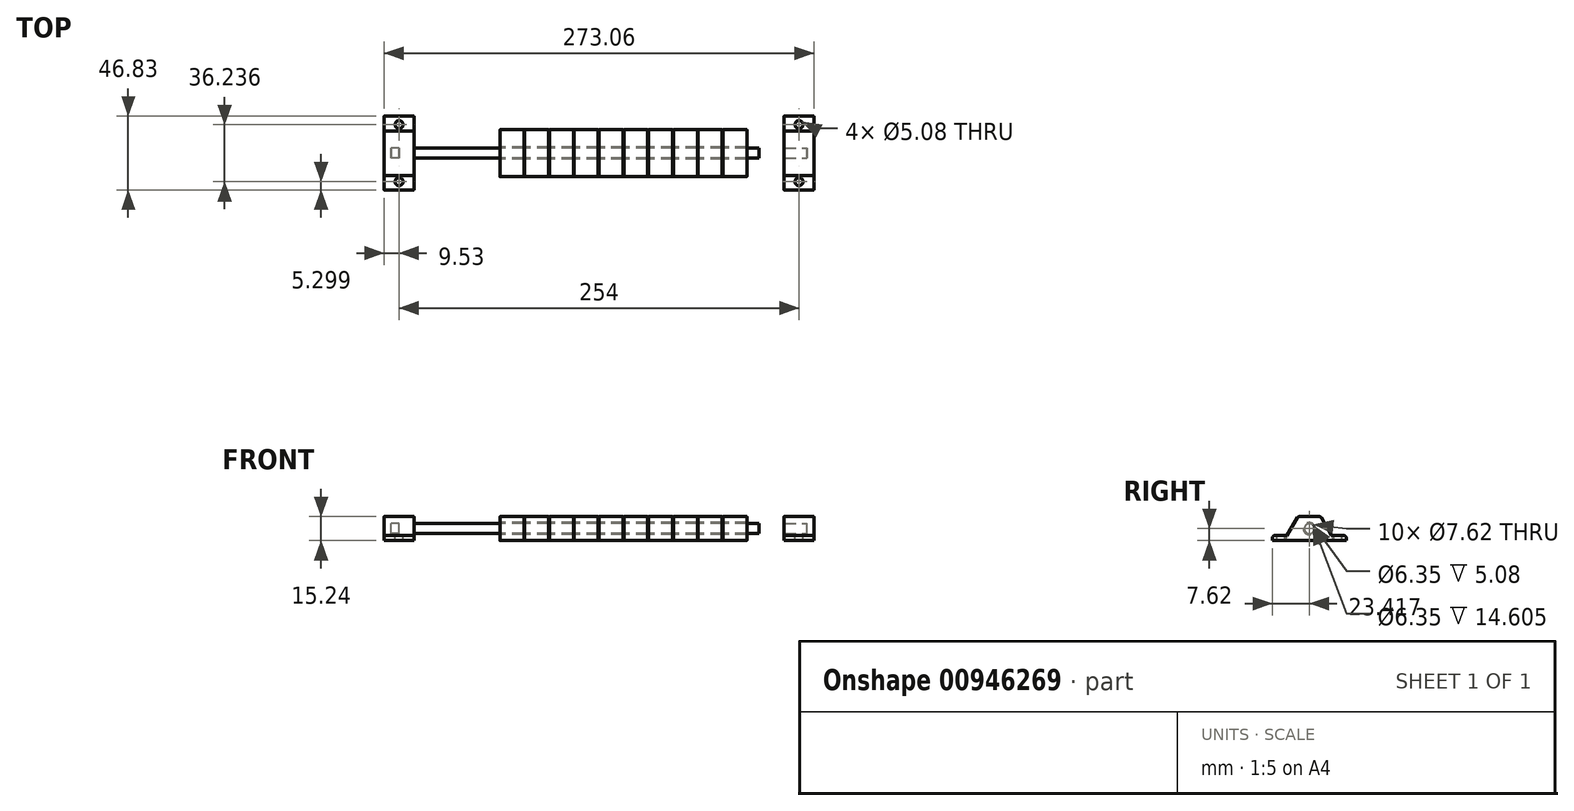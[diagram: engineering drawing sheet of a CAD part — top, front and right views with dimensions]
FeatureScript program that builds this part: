
annotation { "Feature Type Name" : "Feature", "Feature Type Description" : "" }
export const myFeature = defineFeature(function(context is Context, id is Id, definition is map)
    precondition{}
    {
        {
            var Q0;
            Q0=qCreatedBy(makeId("Right.planeOp"),FACE);
            var sketch = newSketch(context, id + "F0", { "sketchPlane" : qUnion([Q0])});
            skLineSegment(sketch, "E0", {"start": v(-49.8, 0) * mm, "end": v(-18.06, 0) * mm});
            skLineSegment(sketch, "E1", {"start": v(-18.06, 0) * mm, "end": v(-26.86, 15.24) * mm});
            skLineSegment(sketch, "E2", {"start": v(-26.86, 15.24) * mm, "end": v(-41, 15.24) * mm});
            skLineSegment(sketch, "E3", {"start": v(-41, 15.24) * mm, "end": v(-49.8, 0) * mm});
            skCircle(sketch, "E4", {"center": v(-33.93, 7.62) * mm, "radius": 3.81 * mm});
            skPoint(sketch, "E4.centerSnap0", {"position": v(-33.93, 15.24) * mm});
            skSolve(sketch);
        }
        {
            var Q0;
            Q0=makeQuery(id+"F0.imprint","IMPRINT",FACE,{"disambiguationData":[TD([[makeQuery(id+"F0.imprint","IMPRINT",EDGE,{"derivedFrom":sQuery(id+"F0.wireOp",EDGE,"E0")}),1.0]])]});
            extrude(context, id + "F1", {"entities" : qUnion([Q0]), "depth" : 15.24 * mm, "offsetDistance" : 25.4 * mm});
        }
        {
            var Q0;
            Q0=makeQuery(id+"F1.opExtrude","SWEPT_EDGE",EDGE,{"disambiguationData":[OSD([sQuery(id+"F0.wireOp",EDGE,"E2"),sQuery(id+"F0.wireOp",EDGE,"E3")])]});
            var Q1;
            Q1=makeQuery(id+"F1.opExtrude","SWEPT_EDGE",EDGE,{"disambiguationData":[OSD([sQuery(id+"F0.wireOp",EDGE,"E1"),sQuery(id+"F0.wireOp",EDGE,"E2")])]});
            var Q2;
            Q2=makeQuery(id+"F1.opExtrude","SWEPT_EDGE",EDGE,{"disambiguationData":[OSD([sQuery(id+"F0.wireOp",EDGE,"E0"),sQuery(id+"F0.wireOp",EDGE,"E1")])]});
            var Q3;
            Q3=makeQuery(id+"F1.opExtrude","SWEPT_EDGE",EDGE,{"disambiguationData":[OSD([sQuery(id+"F0.wireOp",EDGE,"E0"),sQuery(id+"F0.wireOp",EDGE,"E3")])]});
            fillet(context, id + "F2", {"entities" : qUnion([Q0, Q1, Q2, Q3]), "tangentPropagation" : true, "radius" : 1.27 * mm, "defaultsChanged" : true, "vertexSettings" : [], "allowEdgeOverflow" : false});
        }
        {
            var Q0;
            Q0=qCreatedBy(makeId("Right.planeOp"),FACE);
            var sketch = newSketch(context, id + "F3", { "sketchPlane" : qUnion([Q0])});
            skPoint(sketch, "E5.0", {"position": v(-33.93, 7.62) * mm});
            skCircle(sketch, "E6", {"center": v(-33.93, 7.62) * mm, "radius": 3.17 * mm});
            skSolve(sketch);
        }
        {
            var Q0;
            Q0=makeQuery(id+"F3.imprint","IMPRINT",FACE,{"disambiguationData":[TD([[makeQuery(id+"F3.imprint","IMPRINT",EDGE,{"derivedFrom":sQuery(id+"F3.wireOp",EDGE,"E6")}),1.0]])]});
            extrude(context, id + "F4", {"entities" : qUnion([Q0]), "depth" : 254 * mm, "offsetDistance" : 25.4 * mm, "symmetric" : true});
        }
        {
            var Q0;
            Q0=makeQuery(id+"F1.opExtrude","SWEPT_BODY",BODY,{"disambiguationData":[OSD([sQuery(id+"F0.wireOp",EDGE,"E0"),sQuery(id+"F0.wireOp",EDGE,"E1"),sQuery(id+"F0.wireOp",EDGE,"E2"),sQuery(id+"F0.wireOp",EDGE,"E3"),sQuery(id+"F0.wireOp",EDGE,"E4")])]});
            transform(context, id + "F5", {"entities" : qUnion([Q0]), "transformType" : TransformType.TRANSLATION_3D, "dx" : 15.75 * mm, "dy" : 0 * mm, "dz" : 0 * mm, "makeCopy" : true});
        }
        {
            var Q0;
            Q0=makeQuery(id+"F1.opExtrude","SWEPT_BODY",BODY,{"disambiguationData":[OSD([sQuery(id+"F0.wireOp",EDGE,"E0"),sQuery(id+"F0.wireOp",EDGE,"E1"),sQuery(id+"F0.wireOp",EDGE,"E2"),sQuery(id+"F0.wireOp",EDGE,"E3"),sQuery(id+"F0.wireOp",EDGE,"E4")])]});
            var Q1;
            Q1=makeQuery(id+"F5.opPattern","COPY",BODY,{"derivedFrom":makeQuery(id+"F1.opExtrude","SWEPT_BODY",BODY,{"disambiguationData":[OSD([sQuery(id+"F0.wireOp",EDGE,"E0"),sQuery(id+"F0.wireOp",EDGE,"E1"),sQuery(id+"F0.wireOp",EDGE,"E2"),sQuery(id+"F0.wireOp",EDGE,"E3"),sQuery(id+"F0.wireOp",EDGE,"E4")])]}),"instanceName":"1"});
            transform(context, id + "F6", {"entities" : qUnion([Q0, Q1]), "transformType" : TransformType.TRANSLATION_3D, "dx" : 31.5 * mm, "dy" : 0 * mm, "dz" : 0 * mm, "makeCopy" : true});
        }
        {
            var Q0;
            Q0=makeQuery(id+"F1.opExtrude","SWEPT_BODY",BODY,{"disambiguationData":[OSD([sQuery(id+"F0.wireOp",EDGE,"E0"),sQuery(id+"F0.wireOp",EDGE,"E1"),sQuery(id+"F0.wireOp",EDGE,"E2"),sQuery(id+"F0.wireOp",EDGE,"E3"),sQuery(id+"F0.wireOp",EDGE,"E4")])]});
            var Q1;
            Q1=makeQuery(id+"F5.opPattern","COPY",BODY,{"derivedFrom":makeQuery(id+"F1.opExtrude","SWEPT_BODY",BODY,{"disambiguationData":[OSD([sQuery(id+"F0.wireOp",EDGE,"E0"),sQuery(id+"F0.wireOp",EDGE,"E1"),sQuery(id+"F0.wireOp",EDGE,"E2"),sQuery(id+"F0.wireOp",EDGE,"E3"),sQuery(id+"F0.wireOp",EDGE,"E4")])]}),"instanceName":"1"});
            var Q2;
            Q2=makeQuery(id+"F6.opPattern","COPY",BODY,{"derivedFrom":makeQuery(id+"F1.opExtrude","SWEPT_BODY",BODY,{"disambiguationData":[OSD([sQuery(id+"F0.wireOp",EDGE,"E0"),sQuery(id+"F0.wireOp",EDGE,"E1"),sQuery(id+"F0.wireOp",EDGE,"E2"),sQuery(id+"F0.wireOp",EDGE,"E3"),sQuery(id+"F0.wireOp",EDGE,"E4")])]}),"instanceName":"1"});
            var Q3;
            Q3=makeQuery(id+"F6.opPattern","COPY",BODY,{"derivedFrom":makeQuery(id+"F5.opPattern","COPY",BODY,{"derivedFrom":makeQuery(id+"F1.opExtrude","SWEPT_BODY",BODY,{"disambiguationData":[OSD([sQuery(id+"F0.wireOp",EDGE,"E0"),sQuery(id+"F0.wireOp",EDGE,"E1"),sQuery(id+"F0.wireOp",EDGE,"E2"),sQuery(id+"F0.wireOp",EDGE,"E3"),sQuery(id+"F0.wireOp",EDGE,"E4")])]}),"instanceName":"1"}),"instanceName":"1"});
            transform(context, id + "F7", {"entities" : qUnion([Q0, Q1, Q2, Q3]), "transformType" : TransformType.TRANSLATION_3D, "dx" : -63 * mm, "dy" : 0 * mm, "dz" : 0 * mm, "makeCopy" : true});
        }
        {
            var Q0;
            Q0=makeQuery(id+"F1.opExtrude","SWEPT_BODY",BODY,{"disambiguationData":[OSD([sQuery(id+"F0.wireOp",EDGE,"E0"),sQuery(id+"F0.wireOp",EDGE,"E1"),sQuery(id+"F0.wireOp",EDGE,"E2"),sQuery(id+"F0.wireOp",EDGE,"E3"),sQuery(id+"F0.wireOp",EDGE,"E4")])]});
            var Q1;
            Q1=makeQuery(id+"F5.opPattern","COPY",BODY,{"derivedFrom":makeQuery(id+"F1.opExtrude","SWEPT_BODY",BODY,{"disambiguationData":[OSD([sQuery(id+"F0.wireOp",EDGE,"E0"),sQuery(id+"F0.wireOp",EDGE,"E1"),sQuery(id+"F0.wireOp",EDGE,"E2"),sQuery(id+"F0.wireOp",EDGE,"E3"),sQuery(id+"F0.wireOp",EDGE,"E4")])]}),"instanceName":"1"});
            transform(context, id + "F8", {"entities" : qUnion([Q0, Q1]), "transformType" : TransformType.TRANSLATION_3D, "dx" : 63 * mm, "dy" : 0 * mm, "dz" : 0 * mm, "makeCopy" : true});
        }
        {
            var Q0;
            Q0=makeQuery(id+"F4.opExtrude","CAP_FACE",FACE,{"disambiguationData":[OSD([sQuery(id+"F3.wireOp",EDGE,"E6")])],"isStart":false});
            var sketch = newSketch(context, id + "F9", { "sketchPlane" : qUnion([Q0])});
            skPoint(sketch, "E7.0", {"position": v(-33.93, 15.24) * mm});
            skLineSegment(sketch, "E8", {"start": v(-33.93, 0) * mm, "end": v(-10.52, 0) * mm});
            skLineSegment(sketch, "E9", {"start": v(-10.52, 0) * mm, "end": v(-10.52, 3.18) * mm});
            skLineSegment(sketch, "E10", {"start": v(-10.52, 3.18) * mm, "end": v(-19.84, 3.18) * mm});
            skLineSegment(sketch, "E11", {"start": v(-19.84, 3.17) * mm, "end": v(-26.77, 15.24) * mm});
            skLineSegment(sketch, "E12", {"start": v(-26.77, 15.24) * mm, "end": v(-33.93, 15.24) * mm});
            skLineSegment(sketch, "E13", {"start": v(-33.93, 0) * mm, "end": v(-33.93, 15.24) * mm});
            skLineSegment(sketch, "E14.MirrorCS", {"start": v(-41.1, 15.24) * mm, "end": v(-33.93, 15.24) * mm});
            skLineSegment(sketch, "E15.MirrorCS", {"start": v(-57.35, 0) * mm, "end": v(-57.35, 3.18) * mm});
            skLineSegment(sketch, "E16.MirrorCS", {"start": v(-33.93, 0) * mm, "end": v(-57.35, 0) * mm});
            skLineSegment(sketch, "E17.MirrorCS", {"start": v(-48.02, 3.17) * mm, "end": v(-41.1, 15.24) * mm});
            skLineSegment(sketch, "E18.MirrorCS", {"start": v(-57.35, 3.18) * mm, "end": v(-48.02, 3.18) * mm});
            skSolve(sketch);
        }
        {
            var Q0;
            {var subQ4=sQuery(id+"F9.wireOp",EDGE,"E8");Q0=makeQuery(id+"F9.imprint","IMPRINT",FACE,{"disambiguationData":[TD([[makeQuery(id+"F9.imprint","IMPRINT",EDGE,{"derivedFrom":subQ4}),1.0]])]});}
            var Q1;
            {var subQ0=sQuery(id+"F9.wireOp",EDGE,"E14.MirrorCS");Q1=makeQuery(id+"F9.imprint","IMPRINT",FACE,{"disambiguationData":[TD([[makeQuery(id+"F9.imprint","IMPRINT",EDGE,{"derivedFrom":subQ0}),-1.0]])]});}
            var Q2;
            {var subQ0=sQuery(id+"F9.wireOp",EDGE,"E13");var subQ1=makeQuery(id+"F4.opExtrude","CAP_EDGE",EDGE,{"disambiguationData":[OSD([sQuery(id+"F3.wireOp",EDGE,"E6")])],"isStart":false});var subQ2=makeQuery(id+"F9.imprint","INTERSECT",VERTEX,{"disambiguationData":[OD(0.0)],"derivedFrom":[subQ1,subQ0]});Q2=makeQuery(id+"F9.imprint","IMPRINT",FACE,{"disambiguationData":[TD([[makeQuery(id+"F9.imprint","IMPRINT",EDGE,{"disambiguationData":[TD([[subQ2,-1.0]])],"derivedFrom":subQ0}),1.0]])]});}
            var Q3;
            {var subQ0=sQuery(id+"F9.wireOp",EDGE,"E13");var subQ1=makeQuery(id+"F4.opExtrude","CAP_EDGE",EDGE,{"disambiguationData":[OSD([sQuery(id+"F3.wireOp",EDGE,"E6")])],"isStart":false});var subQ2=makeQuery(id+"F9.imprint","INTERSECT",VERTEX,{"disambiguationData":[OD(0.0)],"derivedFrom":[subQ1,subQ0]});Q3=makeQuery(id+"F9.imprint","IMPRINT",FACE,{"disambiguationData":[TD([[makeQuery(id+"F9.imprint","IMPRINT",EDGE,{"disambiguationData":[TD([[subQ2,-1.0]])],"derivedFrom":subQ0}),-1.0]])]});}
            extrude(context, id + "F10", {"entities" : qUnion([Q0, Q1, Q2, Q3]), "oppositeDirection" : true, "depth" : 19.05 * mm, "offsetDistance" : 25.4 * mm, "symmetric" : true});
        }
        {
            var Q0;
            Q0=makeQuery(id+"F10.opExtrude","SWEPT_EDGE",EDGE,{"disambiguationData":[OSD([sQuery(id+"F9.wireOp",EDGE,"E14.MirrorCS"),sQuery(id+"F9.wireOp",EDGE,"E17.MirrorCS")])]});
            var Q1;
            Q1=makeQuery(id+"F10.opExtrude","SWEPT_EDGE",EDGE,{"disambiguationData":[OSD([sQuery(id+"F9.wireOp",EDGE,"E11"),sQuery(id+"F9.wireOp",EDGE,"E12")])]});
            var Q2;
            Q2=makeQuery(id+"F10.opExtrude","SWEPT_EDGE",EDGE,{"disambiguationData":[OSD([sQuery(id+"F9.wireOp",EDGE,"E9"),sQuery(id+"F9.wireOp",EDGE,"E10")])]});
            var Q3;
            Q3=makeQuery(id+"F10.opExtrude","SWEPT_EDGE",EDGE,{"disambiguationData":[OSD([sQuery(id+"F9.wireOp",EDGE,"E15.MirrorCS"),sQuery(id+"F9.wireOp",EDGE,"E18.MirrorCS")])]});
            fillet(context, id + "F11", {"entities" : qUnion([Q0, Q1, Q2, Q3]), "tangentPropagation" : true, "radius" : 1.27 * mm, "defaultsChanged" : true, "vertexSettings" : [], "allowEdgeOverflow" : false});
        }
        {
            var Q0;
            Q0=makeQuery(id+"F4.opExtrude","CAP_FACE",FACE,{"disambiguationData":[OSD([sQuery(id+"F3.wireOp",EDGE,"E6")])],"isStart":false});
            extrude(context, id + "F12", {"entities" : qUnion([Q0]), "operationType" : NewBodyOperationType.REMOVE, "oppositeDirection" : true, "depth" : 25.4 * mm, "offsetDistance" : 25.4 * mm});
        }
        {
            var Q0;
            Q0=makeQuery(id+"F12.boolean.opBoolean","COPY",FACE,{"derivedFrom":makeQuery(id+"F12.opExtrude","CAP_FACE",FACE,{"disambiguationData":[OSD([sQuery(id+"F3.wireOp",EDGE,"E6")])],"isStart":true})});
            extrude(context, id + "F13", {"entities" : qUnion([Q0]), "operationType" : NewBodyOperationType.REMOVE, "oppositeDirection" : true, "depth" : 5.08 * mm, "offsetDistance" : 25.4 * mm});
        }
        {
            var Q0;
            Q0=makeQuery(id+"F10.opExtrude","SWEPT_FACE",FACE,{"disambiguationData":[OSD([sQuery(id+"F9.wireOp",EDGE,"E10")])]});
            var sketch = newSketch(context, id + "F14", { "sketchPlane" : qUnion([Q0])});
            skLineSegment(sketch, "E19.0.0", {"start": v(136.53, -19.84) * mm, "end": v(136.53, -11.79) * mm});
            skLineSegment(sketch, "E19.0.1", {"start": v(136.53, -11.79) * mm, "end": v(117.48, -11.79) * mm});
            skLineSegment(sketch, "E19.0.2", {"start": v(117.48, -11.79) * mm, "end": v(117.48, -19.84) * mm});
            skLineSegment(sketch, "E19.0.3", {"start": v(117.48, -19.84) * mm, "end": v(136.53, -19.84) * mm});
            skLineSegment(sketch, "E20.0.0", {"start": v(117.48, -48.02) * mm, "end": v(117.48, -56.08) * mm});
            skLineSegment(sketch, "E20.0.1", {"start": v(117.48, -56.08) * mm, "end": v(136.53, -56.08) * mm});
            skLineSegment(sketch, "E20.0.2", {"start": v(136.53, -56.08) * mm, "end": v(136.53, -48.02) * mm});
            skLineSegment(sketch, "E20.0.3", {"start": v(136.53, -48.02) * mm, "end": v(117.48, -48.02) * mm});
            skCircle(sketch, "E21", {"center": v(127, -15.81) * mm, "radius": 2.54 * mm});
            skPoint(sketch, "E21.centerSnap0", {"position": v(117.48, -15.81) * mm});
            skPoint(sketch, "E21.centerSnap1", {"position": v(127, -11.79) * mm});
            skCircle(sketch, "E22", {"center": v(127, -52.05) * mm, "radius": 2.54 * mm});
            skPoint(sketch, "E22.centerSnap0", {"position": v(136.53, -52.05) * mm});
            skPoint(sketch, "E22.centerSnap1", {"position": v(127, -56.08) * mm});
            skSolve(sketch);
        }
        {
            var Q0;
            Q0=makeQuery(id+"F14.imprint","IMPRINT",FACE,{"disambiguationData":[TD([[makeQuery(id+"F14.imprint","IMPRINT",EDGE,{"derivedFrom":sQuery(id+"F14.wireOp",EDGE,"E21")}),1.0]])]});
            var Q1;
            Q1=makeQuery(id+"F14.imprint","IMPRINT",FACE,{"disambiguationData":[TD([[makeQuery(id+"F14.imprint","IMPRINT",EDGE,{"derivedFrom":sQuery(id+"F14.wireOp",EDGE,"E22")}),1.0]])]});
            extrude(context, id + "F15", {"entities" : qUnion([Q0, Q1]), "operationType" : NewBodyOperationType.REMOVE, "oppositeDirection" : true, "depth" : 25.4 * mm, "offsetDistance" : 25.4 * mm});
        }
        {
            var Q0;
            Q0=makeQuery(id+"F10.opExtrude","SWEPT_BODY",BODY,{"disambiguationData":[OSD([sQuery(id+"F9.wireOp",EDGE,"E8"),sQuery(id+"F9.wireOp",EDGE,"E9"),sQuery(id+"F9.wireOp",EDGE,"E10"),sQuery(id+"F9.wireOp",EDGE,"E11"),sQuery(id+"F9.wireOp",EDGE,"E12"),sQuery(id+"F9.wireOp",EDGE,"E14.MirrorCS"),sQuery(id+"F9.wireOp",EDGE,"E15.MirrorCS"),sQuery(id+"F9.wireOp",EDGE,"E16.MirrorCS"),sQuery(id+"F9.wireOp",EDGE,"E17.MirrorCS"),sQuery(id+"F9.wireOp",EDGE,"E18.MirrorCS")])]});
            var Q1;
            Q1=qCreatedBy(makeId("Right.planeOp"),FACE);
            mirror(context, id + "F16", {"operationType" : NewBodyOperationType.ADD, "entities" : qUnion([Q0]), "mirrorPlane" : qUnion([Q1])});
        }
    });
